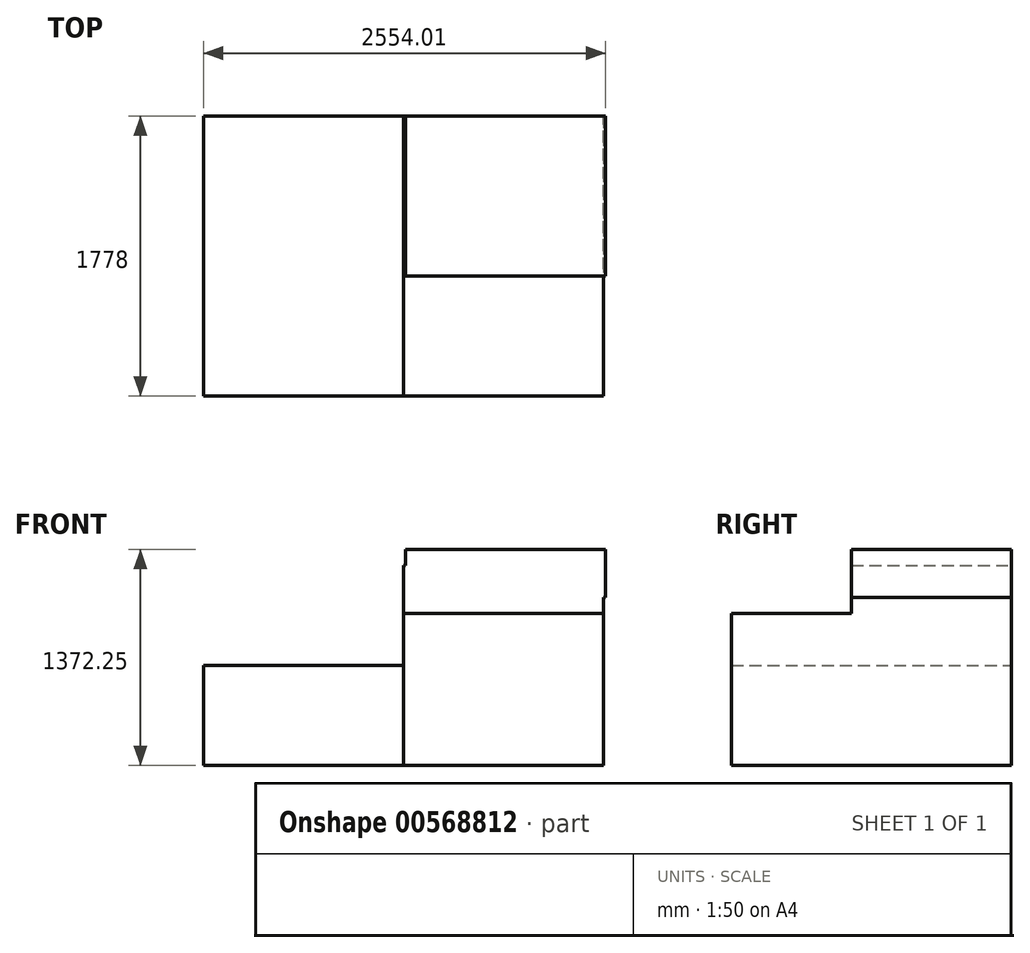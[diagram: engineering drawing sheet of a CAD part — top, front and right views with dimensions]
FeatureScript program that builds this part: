
annotation { "Feature Type Name" : "Feature", "Feature Type Description" : "" }
export const myFeature = defineFeature(function(context is Context, id is Id, definition is map)
    precondition{}
    {
        {
            var Q0;
            Q0=qCreatedBy(makeId("Front.planeOp"),FACE);
            var sketch = newSketch(context, id + "F0", { "sketchPlane" : qUnion([Q0])});
            skLineSegment(sketch, "E0.bottom", {"start": v(-1762.35, -432.45) * mm, "end": v(-492.35, -432.45) * mm});
            skLineSegment(sketch, "E0.top", {"start": v(-1762.35, -1067.45) * mm, "end": v(-492.35, -1067.45) * mm});
            skLineSegment(sketch, "E0.left", {"start": v(-1762.35, -432.45) * mm, "end": v(-1762.35, -1067.45) * mm});
            skLineSegment(sketch, "E0.right", {"start": v(-492.35, -432.45) * mm, "end": v(-492.35, -1067.45) * mm});
            skSolve(sketch);
        }
        {
            var Q0;
            Q0=qCreatedBy(makeId("Front.planeOp"),FACE);
            var sketch = newSketch(context, id + "F1", { "sketchPlane" : qUnion([Q0])});
            skLineSegment(sketch, "E1.bottom", {"start": v(-492.35, -1067.45) * mm, "end": v(777.65, -1067.45) * mm});
            skLineSegment(sketch, "E1.top", {"start": v(-492.35, -102.25) * mm, "end": v(777.65, -102.25) * mm});
            skLineSegment(sketch, "E1.left", {"start": v(-492.35, -1067.45) * mm, "end": v(-492.35, -102.25) * mm});
            skLineSegment(sketch, "E1.right", {"start": v(777.65, -1067.45) * mm, "end": v(777.65, -102.25) * mm});
            skSolve(sketch);
        }
        {
            var Q0;
            Q0=makeQuery(id+"F1.imprint","IMPRINT",FACE,{"disambiguationData":[TD([[makeQuery(id+"F1.imprint","IMPRINT",EDGE,{"derivedFrom":sQuery(id+"F1.wireOp",EDGE,"E1.bottom")}),1.0]])]});
            extrude(context, id + "F2", {"entities" : qUnion([Q0]), "depth" : 1778 * mm, "offsetDistance" : 25.4 * mm});
        }
        {
            var Q0;
            Q0=makeQuery(id+"F0.imprint","IMPRINT",FACE,{"disambiguationData":[TD([[makeQuery(id+"F0.imprint","IMPRINT",EDGE,{"derivedFrom":sQuery(id+"F0.wireOp",EDGE,"E0.bottom")}),-1.0]])]});
            extrude(context, id + "F3", {"entities" : qUnion([Q0]), "depth" : 1778 * mm, "offsetDistance" : 25.4 * mm});
        }
        {
            var Q0;
            Q0=qCreatedBy(makeId("Top.planeOp"),FACE);
            var sketch = newSketch(context, id + "F4", { "sketchPlane" : qUnion([Q0])});
            skLineSegment(sketch, "E2.bottom", {"start": v(-478.34, 0) * mm, "end": v(791.66, 0) * mm});
            skLineSegment(sketch, "E2.top", {"start": v(-478.34, -1016) * mm, "end": v(791.66, -1016) * mm});
            skLineSegment(sketch, "E2.left", {"start": v(-478.34, 0) * mm, "end": v(-478.34, -1016) * mm});
            skLineSegment(sketch, "E2.right", {"start": v(791.66, 0) * mm, "end": v(791.66, -1016) * mm});
            skSolve(sketch);
        }
        {
            var Q0;
            Q0=makeQuery(id+"F4.imprint","IMPRINT",FACE,{"disambiguationData":[TD([[makeQuery(id+"F4.imprint","IMPRINT",EDGE,{"derivedFrom":sQuery(id+"F4.wireOp",EDGE,"E2.bottom")}),-1.0]])]});
            extrude(context, id + "F5", {"entities" : qUnion([Q0]), "operationType" : NewBodyOperationType.ADD, "depth" : 304.8 * mm, "offsetDistance" : 25.4 * mm});
        }
        {
            var Q0;
            Q0=makeQuery(id+"F2.opExtrude","SWEPT_FACE",FACE,{"disambiguationData":[OSD([sQuery(id+"F1.wireOp",EDGE,"E1.top")])]});
            var sketch = newSketch(context, id + "F6", { "sketchPlane" : qUnion([Q0])});
            skLineSegment(sketch, "E3.bottom", {"start": v(-492.35, 0) * mm, "end": v(777.65, 0) * mm});
            skLineSegment(sketch, "E3.top", {"start": v(-492.35, -1016) * mm, "end": v(777.65, -1016) * mm});
            skLineSegment(sketch, "E3.left", {"start": v(-492.35, 0) * mm, "end": v(-492.35, -1016) * mm});
            skLineSegment(sketch, "E3.right", {"start": v(777.65, 0) * mm, "end": v(777.65, -1016) * mm});
            skSolve(sketch);
        }
        {
            var Q0;
            Q0=makeQuery(id+"F6.imprint","IMPRINT",FACE,{"disambiguationData":[TD([[makeQuery(id+"F6.imprint","IMPRINT",EDGE,{"derivedFrom":sQuery(id+"F6.wireOp",EDGE,"E3.bottom")}),-1.0]])]});
            extrude(context, id + "F7", {"entities" : qUnion([Q0]), "operationType" : NewBodyOperationType.ADD, "depth" : 304.8 * mm, "offsetDistance" : 25.4 * mm});
        }
    });
